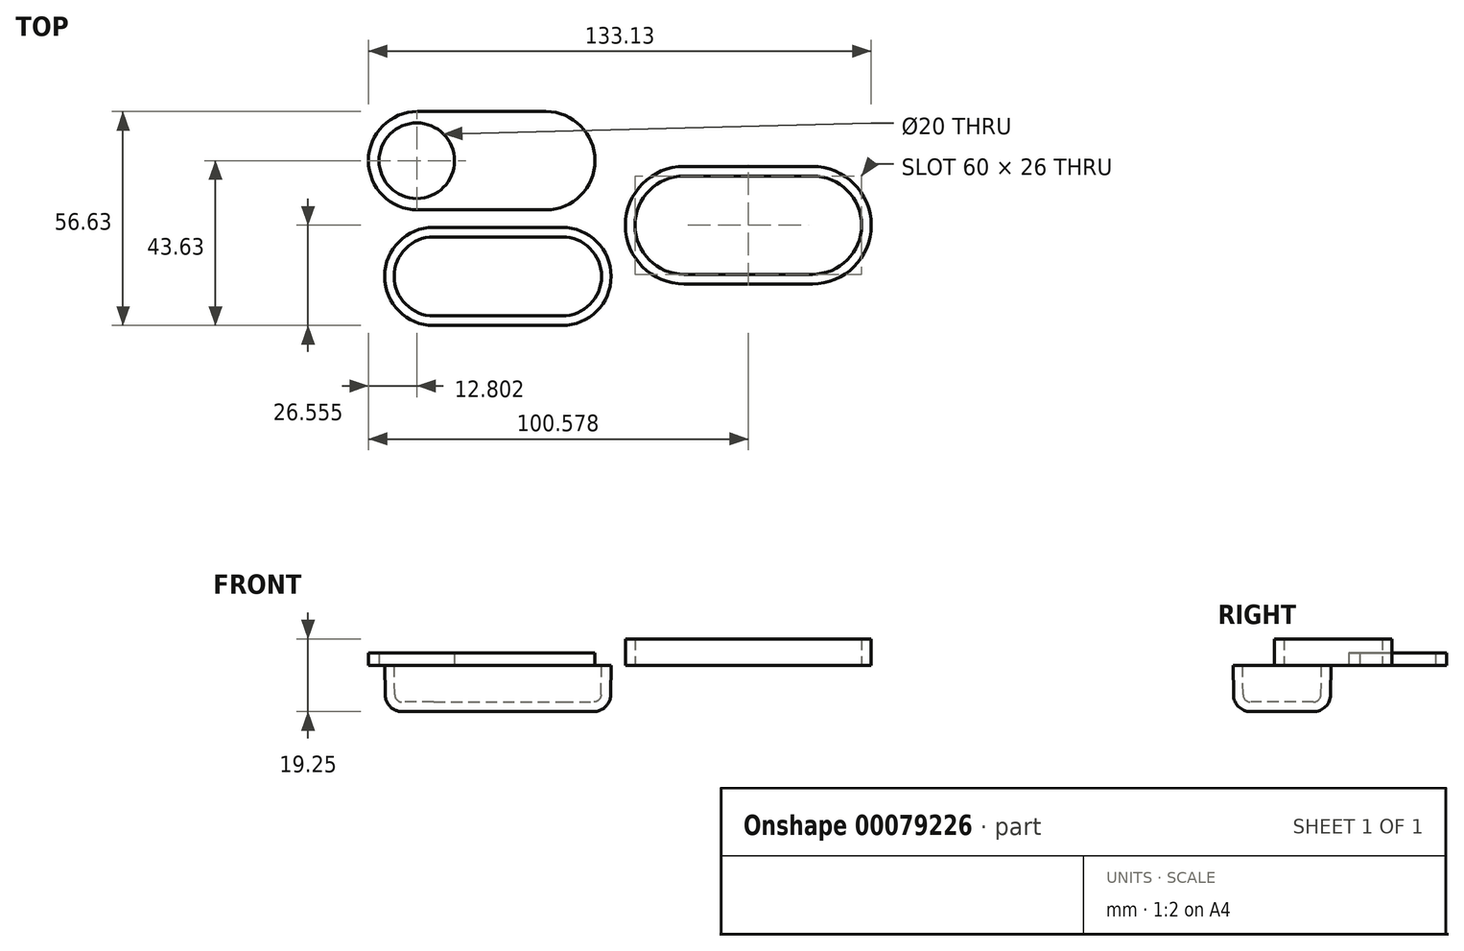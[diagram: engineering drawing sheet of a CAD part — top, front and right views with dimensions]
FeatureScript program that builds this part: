
annotation { "Feature Type Name" : "Feature", "Feature Type Description" : "" }
export const myFeature = defineFeature(function(context is Context, id is Id, definition is map)
    precondition{}
    {
        {
            var Q0;
            Q0=qCreatedBy(makeId("Top.planeOp"),FACE);
            var sketch = newSketch(context, id + "F0", { "sketchPlane" : qUnion([Q0])});
            skLineSegment(sketch, "E0.bottom", {"start": v(0, 0) * mm, "end": v(-60, 0) * mm});
            skLineSegment(sketch, "E0.top", {"start": v(0, -26) * mm, "end": v(-60, -26) * mm});
            skLineSegment(sketch, "E0.left", {"start": v(0, 0) * mm, "end": v(0, -26) * mm});
            skLineSegment(sketch, "E0.right", {"start": v(-60, 0) * mm, "end": v(-60, -26) * mm});
            skCircle(sketch, "E1", {"center": v(-47, -13) * mm, "radius": 13 * mm});
            skCircle(sketch, "E2", {"center": v(-13, -13) * mm, "radius": 13 * mm});
            skSolve(sketch);
        }
        {
            var Q0;
            {var subQ0=sQuery(id+"F0.wireOp",EDGE,"E1");var subQ1=makeQuery(id+"F0.imprint","INTERSECT",VERTEX,{"derivedFrom":[sQuery(id+"F0.wireOp",EDGE,"E0.bottom"),subQ0]});Q0=makeQuery(id+"F0.imprint","IMPRINT",FACE,{"disambiguationData":[TD([[makeQuery(id+"F0.imprint","IMPRINT",EDGE,{"disambiguationData":[TD([[subQ1,-1.0]])],"derivedFrom":subQ0}),1.0]])]});}
            var Q1;
            {var subQ0=sQuery(id+"F0.wireOp",EDGE,"E2");var subQ1=sQuery(id+"F0.wireOp",EDGE,"E0.bottom");var subQ2=makeQuery(id+"F0.imprint","INTERSECT",VERTEX,{"derivedFrom":[subQ1,subQ0]});Q1=makeQuery(id+"F0.imprint","IMPRINT",FACE,{"disambiguationData":[TD([[makeQuery(id+"F0.imprint","IMPRINT",EDGE,{"disambiguationData":[TD([[subQ2,-1.0]])],"derivedFrom":subQ1}),1.0]])]});}
            var Q2;
            {var subQ0=sQuery(id+"F0.wireOp",EDGE,"E2");var subQ1=makeQuery(id+"F0.imprint","INTERSECT",VERTEX,{"derivedFrom":[sQuery(id+"F0.wireOp",EDGE,"E0.bottom"),subQ0]});Q2=makeQuery(id+"F0.imprint","IMPRINT",FACE,{"disambiguationData":[TD([[makeQuery(id+"F0.imprint","IMPRINT",EDGE,{"disambiguationData":[TD([[subQ1,1.0]])],"derivedFrom":subQ0}),1.0]])]});}
            extrude(context, id + "F1", {"entities" : qUnion([Q0, Q1, Q2]), "oppositeDirection" : true, "depth" : 12.2 * mm, "hasDraft" : true, "draftAngle" : 1 * degree, "draftPullDirection" : true});
        }
        {
            var Q0;
            Q0=makeQuery(id+"F1.opExtrude","CAP_FACE",FACE,{"disambiguationData":[OSD([sQuery(id+"F0.wireOp",EDGE,"E0.bottom"),sQuery(id+"F0.wireOp",EDGE,"E0.top"),sQuery(id+"F0.wireOp",EDGE,"E1"),sQuery(id+"F0.wireOp",EDGE,"E2")])],"isStart":false});
            fillet(context, id + "F2", {"entities" : qUnion([Q0]), "radius" : 4.57 * mm, "tangentPropagation" : true, "allowEdgeOverflow" : false});
        }
        {
            var Q0;
            Q0=qCreatedBy(makeId("Top.planeOp"),FACE);
            var sketch = newSketch(context, id + "F3", { "sketchPlane" : qUnion([Q0])});
            skLineSegment(sketch, "E3.bottom", {"start": v(-4.27, 30.63) * mm, "end": v(-64.27, 30.63) * mm});
            skLineSegment(sketch, "E3.top", {"start": v(-4.27, 4.63) * mm, "end": v(-64.27, 4.63) * mm});
            skLineSegment(sketch, "E3.left", {"start": v(-4.27, 30.63) * mm, "end": v(-4.27, 4.63) * mm});
            skLineSegment(sketch, "E3.right", {"start": v(-64.27, 30.63) * mm, "end": v(-64.27, 4.63) * mm});
            skCircle(sketch, "E4", {"center": v(-51.27, 17.63) * mm, "radius": 13 * mm});
            skCircle(sketch, "E5", {"center": v(-17.27, 17.63) * mm, "radius": 13 * mm});
            skCircle(sketch, "E6", {"center": v(-51.47, 17.63) * mm, "radius": 10 * mm});
            skPoint(sketch, "E7", {"position": v(-64.27, 17.63) * mm});
            skLineSegment(sketch, "E8", {"start": v(-64.27, 17.63) * mm, "end": v(-61.47, 17.63) * mm, "construction": true});
            skSolve(sketch);
        }
        {
            var Q0;
            {var subQ0=sQuery(id+"F3.wireOp",EDGE,"E5");var subQ1=makeQuery(id+"F3.imprint","INTERSECT",VERTEX,{"derivedFrom":[sQuery(id+"F3.wireOp",EDGE,"E3.bottom"),subQ0]});Q0=makeQuery(id+"F3.imprint","IMPRINT",FACE,{"disambiguationData":[TD([[makeQuery(id+"F3.imprint","IMPRINT",EDGE,{"disambiguationData":[TD([[subQ1,1.0]])],"derivedFrom":subQ0}),1.0]])]});}
            var Q1;
            Q1=makeQuery(id+"F3.imprint","IMPRINT",FACE,{"disambiguationData":[TD([[makeQuery(id+"F3.imprint","IMPRINT",EDGE,{"derivedFrom":sQuery(id+"F3.wireOp",EDGE,"E6")}),-1.0]])]});
            var Q2;
            {var subQ0=sQuery(id+"F3.wireOp",EDGE,"E5");var subQ1=sQuery(id+"F3.wireOp",EDGE,"E3.bottom");var subQ2=makeQuery(id+"F3.imprint","INTERSECT",VERTEX,{"derivedFrom":[subQ1,subQ0]});Q2=makeQuery(id+"F3.imprint","IMPRINT",FACE,{"disambiguationData":[TD([[makeQuery(id+"F3.imprint","IMPRINT",EDGE,{"disambiguationData":[TD([[subQ2,-1.0]])],"derivedFrom":subQ1}),1.0]])]});}
            extrude(context, id + "F4", {"entities" : qUnion([Q0, Q1, Q2]), "depth" : 3.4 * mm});
        }
        {
            var Q0;
            Q0=makeQuery(id+"F1.opExtrude","CAP_FACE",FACE,{"disambiguationData":[OSD([sQuery(id+"F0.wireOp",EDGE,"E0.bottom"),sQuery(id+"F0.wireOp",EDGE,"E0.top"),sQuery(id+"F0.wireOp",EDGE,"E1"),sQuery(id+"F0.wireOp",EDGE,"E2")])],"isStart":true});
            shell(context, id + "F5", {"entities" : qUnion([Q0]), "thickness" : 2.54 * mm});
        }
        {
            var Q0;
            Q0=qCreatedBy(makeId("Top.planeOp"),FACE);
            var sketch = newSketch(context, id + "F6", { "sketchPlane" : qUnion([Q0])});
            skLineSegment(sketch, "E9.bottom", {"start": v(53.3, 13.56) * mm, "end": v(19.3, 13.56) * mm});
            skLineSegment(sketch, "E9.top", {"start": v(53.3, -12.44) * mm, "end": v(19.3, -12.44) * mm});
            skArc(sketch, "E10", {"start": v(19.3, 13.56) * mm, "mid": v(6.3, 0.56) * mm, "end": v(19.3, -12.44) * mm});
            skArc(sketch, "E11", {"start": v(53.3, -12.44) * mm, "mid": v(66.3, 0.56) * mm, "end": v(53.3, 13.56) * mm});
            skLineSegment(sketch, "E12.0", {"start": v(53.3, 16.1) * mm, "end": v(19.3, 16.1) * mm});
            skArc(sketch, "E12.1", {"start": v(53.3, -15) * mm, "mid": v(68.86, 0.56) * mm, "end": v(53.3, 16.1) * mm});
            skLineSegment(sketch, "E12.2", {"start": v(53.3, -15) * mm, "end": v(19.3, -15) * mm});
            skArc(sketch, "E12.3", {"start": v(19.3, 16.1) * mm, "mid": v(3.76, 0.56) * mm, "end": v(19.3, -15) * mm});
            skSolve(sketch);
        }
        {
            var Q0;
            Q0=makeQuery(id+"F6.imprint","IMPRINT",FACE,{"disambiguationData":[TD([[makeQuery(id+"F6.imprint","IMPRINT",EDGE,{"derivedFrom":sQuery(id+"F6.wireOp",EDGE,"E9.bottom")}),-1.0]])]});
            extrude(context, id + "F7", {"entities" : qUnion([Q0]), "depth" : 7.05 * mm});
        }
    });
